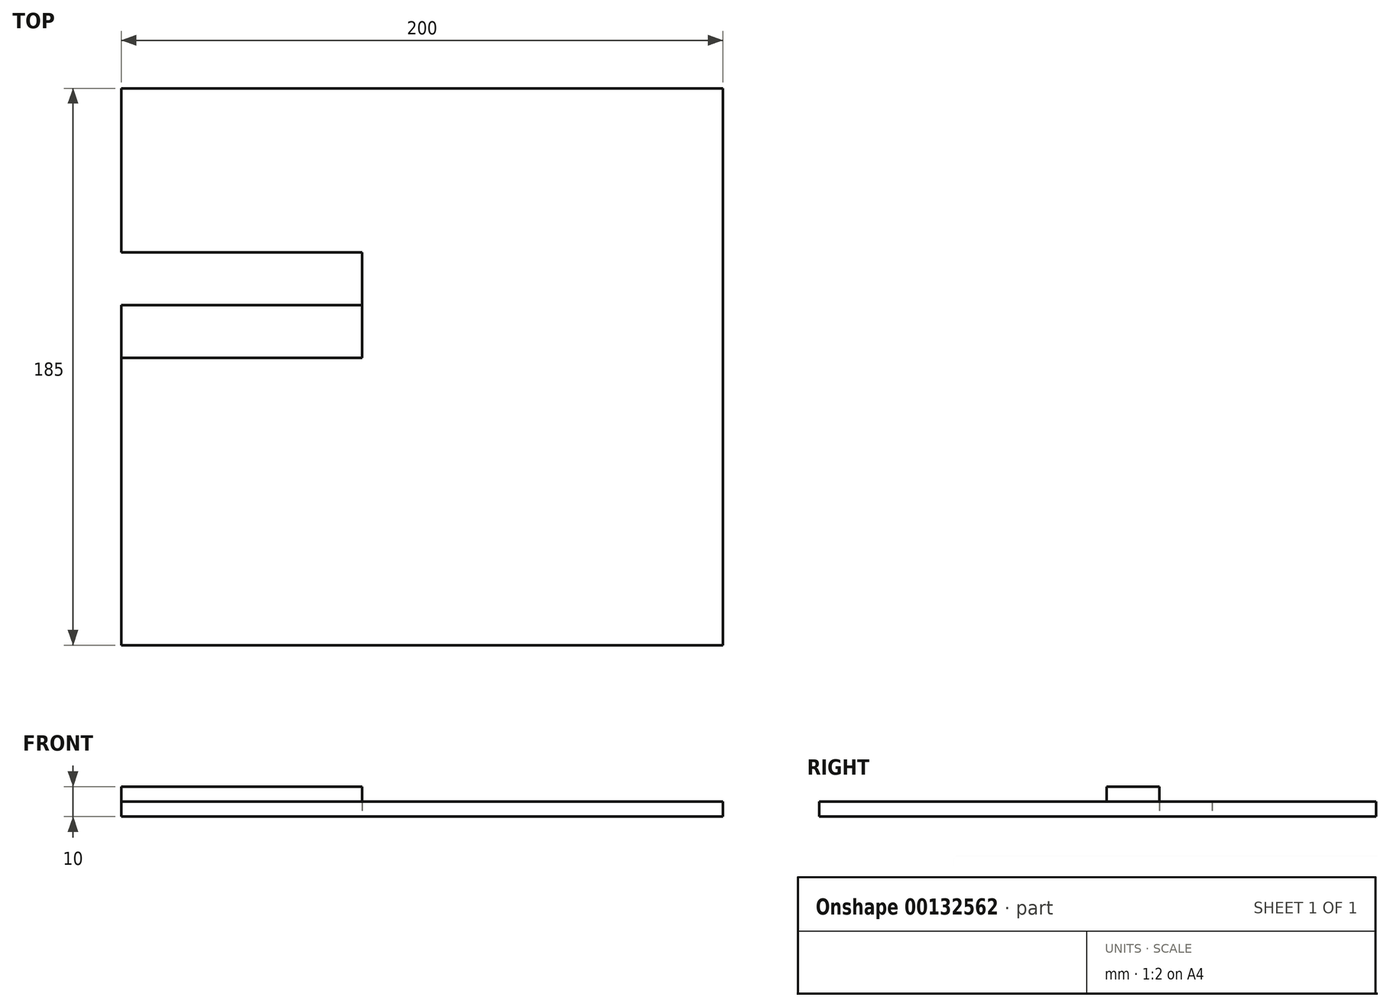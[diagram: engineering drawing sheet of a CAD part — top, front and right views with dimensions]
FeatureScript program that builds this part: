
annotation { "Feature Type Name" : "Feature", "Feature Type Description" : "" }
export const myFeature = defineFeature(function(context is Context, id is Id, definition is map)
    precondition{}
    {
        {
            var Q0;
            Q0=qCreatedBy(makeId("Top.planeOp"),FACE);
            var sketch = newSketch(context, id + "F0", { "sketchPlane" : qUnion([Q0])});
            skLineSegment(sketch, "E0.bottom", {"start": v(65.61, -69.82) * mm, "end": v(-134.39, -69.82) * mm});
            skLineSegment(sketch, "E0.top", {"start": v(65.62, 115.18) * mm, "end": v(-134.38, 115.18) * mm});
            skLineSegment(sketch, "E0.left", {"start": v(65.62, -69.82) * mm, "end": v(65.62, 115.18) * mm});
            skLineSegment(sketch, "E0.right", {"start": v(-134.38, -69.82) * mm, "end": v(-134.38, 115.18) * mm});
            skPoint(sketch, "E0.middle", {"position": v(-34.38, 22.68) * mm});
            skPoint(sketch, "E1.middle", {"position": v(-71.64, 22.84) * mm});
            skLineSegment(sketch, "E2.bottom", {"start": v(-54.39, 25.68) * mm, "end": v(-134.38, 25.68) * mm});
            skLineSegment(sketch, "E2.top", {"start": v(-54.39, 60.68) * mm, "end": v(-134.38, 60.68) * mm});
            skLineSegment(sketch, "E2.left", {"start": v(-54.39, 25.68) * mm, "end": v(-54.39, 60.68) * mm});
            skLineSegment(sketch, "E2.right", {"start": v(-134.38, 25.68) * mm, "end": v(-134.38, 60.68) * mm});
            skLineSegment(sketch, "E3", {"start": v(-54.39, 43.18) * mm, "end": v(-134.38, 43.18) * mm});
            skSolve(sketch);
        }
        {
            var Q0;
            {var subQ1=sQuery(id+"F0.wireOp",EDGE,"E0.bottom");Q0=makeQuery(id+"F0.imprint","IMPRINT",FACE,{"disambiguationData":[TD([[makeQuery(id+"F0.imprint","IMPRINT",EDGE,{"derivedFrom":subQ1}),-1.0]])]});}
            extrude(context, id + "F1", {"entities" : qUnion([Q0]), "depth" : 5 * mm});
        }
        {
            var Q0;
            Q0=makeQuery(id+"F0.imprint","IMPRINT",FACE,{"disambiguationData":[TD([[makeQuery(id+"F0.imprint","IMPRINT",EDGE,{"derivedFrom":sQuery(id+"F0.wireOp",EDGE,"E2.bottom")}),-1.0]])]});
            extrude(context, id + "F2", {"entities" : qUnion([Q0]), "operationType" : NewBodyOperationType.ADD, "depth" : 10 * mm});
        }
    });
